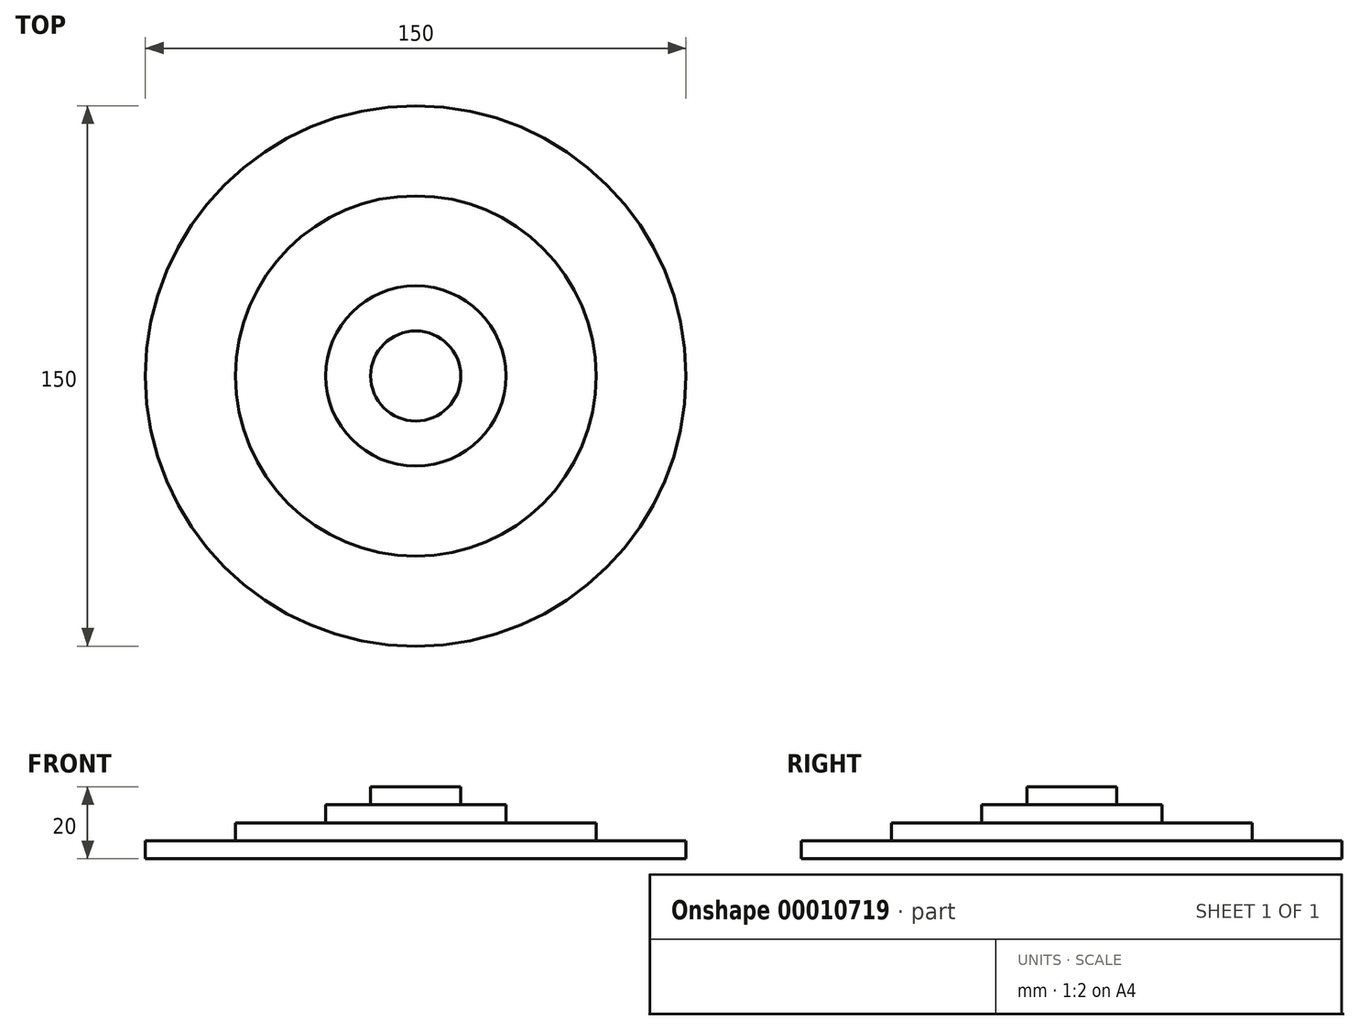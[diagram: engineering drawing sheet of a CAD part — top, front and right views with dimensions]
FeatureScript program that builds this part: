
annotation { "Feature Type Name" : "Feature", "Feature Type Description" : "" }
export const myFeature = defineFeature(function(context is Context, id is Id, definition is map)
    precondition{}
    {
        {
            var Q0;
            Q0=qCreatedBy(makeId("Top.planeOp"),FACE);
            var sketch = newSketch(context, id + "F5", { "sketchPlane" : qUnion([Q0])});
            skCircle(sketch, "E0", {"center": v(0, 0) * mm, "radius": 75 * mm});
            skSolve(sketch);
        }
        {
            var Q0;
            Q0 = qSketchRegion(id + "F5", true);
            extrude(context, id + "F0", {"entities" : qUnion([Q0]), "depth" : 5 * mm});
        }
        {
            var Q0;
            Q0=makeQuery(id+"F0.opExtrude","CAP_FACE",FACE,{"disambiguationData":[OSD([sQuery(id+"F5.wireOp",EDGE,"E0")])],"isStart":false});
            var sketch = newSketch(context, id + "F1", { "sketchPlane" : qUnion([Q0])});
            skCircle(sketch, "E1", {"center": v(0, 0) * mm, "radius": 50 * mm});
            skSolve(sketch);
        }
        {
            var Q0;
            Q0 = qSketchRegion(id + "F1", true);
            extrude(context, id + "F2", {"entities" : qUnion([Q0]), "operationType" : NewBodyOperationType.ADD, "depth" : 5 * mm});
        }
        {
            var Q0;
            Q0=makeQuery(id+"F2.opExtrude","CAP_FACE",FACE,{"disambiguationData":[OSD([sQuery(id+"F1.wireOp",EDGE,"E1")])],"isStart":false});
            var sketch = newSketch(context, id + "F6", { "sketchPlane" : qUnion([Q0])});
            skCircle(sketch, "E2", {"center": v(0, 0) * mm, "radius": 25 * mm});
            skSolve(sketch);
        }
        {
            var Q0;
            Q0 = qSketchRegion(id + "F6", true);
            extrude(context, id + "F3", {"entities" : qUnion([Q0]), "operationType" : NewBodyOperationType.ADD, "depth" : 5 * mm});
        }
        {
            var Q0;
            Q0=makeQuery(id+"F3.opExtrude","CAP_FACE",FACE,{"disambiguationData":[OSD([sQuery(id+"F6.wireOp",EDGE,"E2")])],"isStart":false});
            var sketch = newSketch(context, id + "F7", { "sketchPlane" : qUnion([Q0])});
            skCircle(sketch, "E3", {"center": v(0, 0) * mm, "radius": 12.5 * mm});
            skSolve(sketch);
        }
        {
            var Q0;
            Q0=makeQuery(id+"F7.imprint","IMPRINT",FACE,{"disambiguationData":[TD([[makeQuery(id+"F7.imprint","IMPRINT",EDGE,{"derivedFrom":sQuery(id+"F7.wireOp",EDGE,"E3")}),1.0]])]});
            extrude(context, id + "F4", {"entities" : qUnion([Q0]), "operationType" : NewBodyOperationType.ADD, "depth" : 5 * mm});
        }
    });
